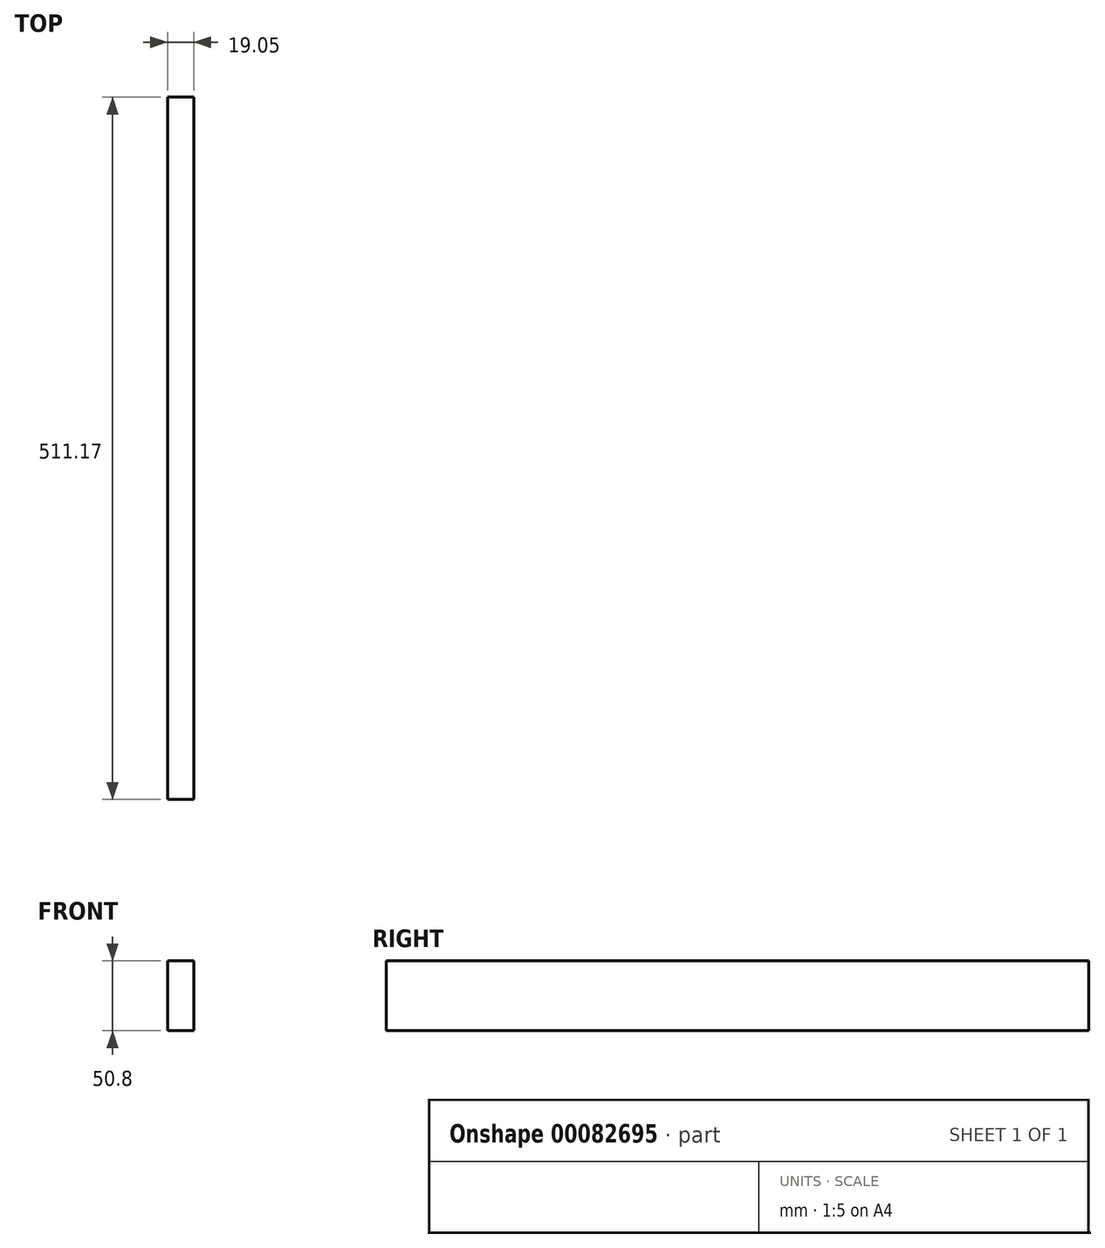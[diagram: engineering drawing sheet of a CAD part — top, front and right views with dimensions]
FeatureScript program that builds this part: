
annotation { "Feature Type Name" : "Feature", "Feature Type Description" : "" }
export const myFeature = defineFeature(function(context is Context, id is Id, definition is map)
    precondition{}
    {
        {
            var Q0;
            Q0=qCreatedBy(makeId("Right.planeOp"),FACE);
            var sketch = newSketch(context, id + "F0", { "sketchPlane" : qUnion([Q0])});
            skLineSegment(sketch, "E0.bottom", {"start": v(-47.1, -77.72) * mm, "end": v(464.08, -77.72) * mm});
            skLineSegment(sketch, "E0.top", {"start": v(-47.1, -128.52) * mm, "end": v(464.08, -128.52) * mm});
            skLineSegment(sketch, "E0.left", {"start": v(-47.1, -77.72) * mm, "end": v(-47.1, -128.52) * mm});
            skLineSegment(sketch, "E0.right", {"start": v(464.08, -77.72) * mm, "end": v(464.08, -128.52) * mm});
            skSolve(sketch);
        }
        {
            var Q0;
            Q0=qSketchRegion(id+"F0",true);
            extrude(context, id + "F1", {"entities" : qUnion([Q0]), "depth" : 19.05 * mm});
        }
    });
